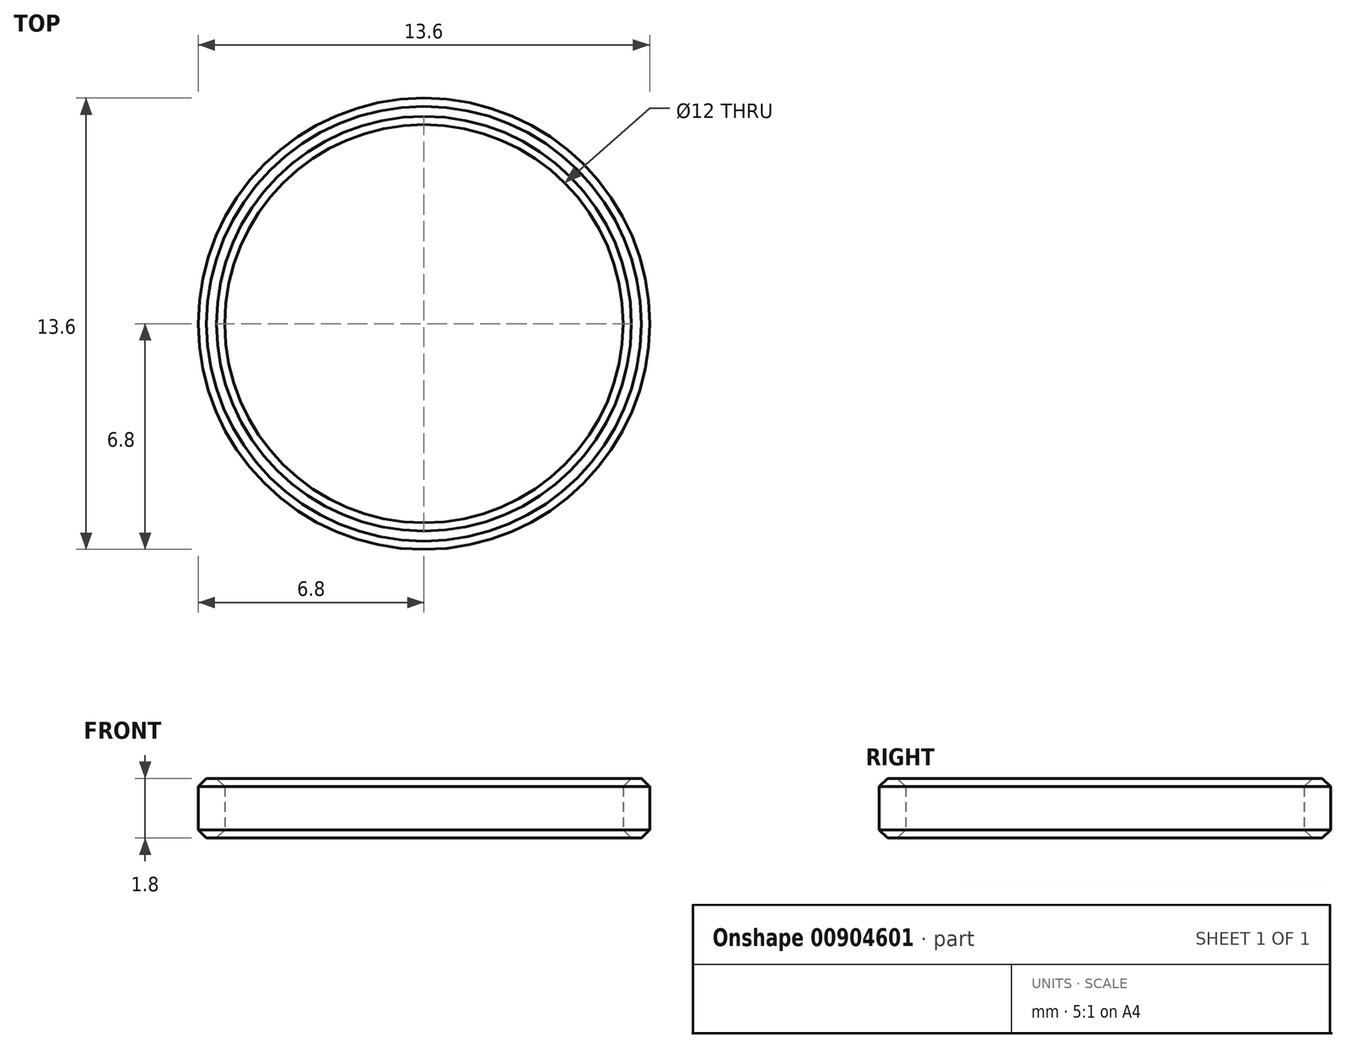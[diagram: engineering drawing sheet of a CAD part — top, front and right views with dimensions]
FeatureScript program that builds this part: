
annotation { "Feature Type Name" : "Feature", "Feature Type Description" : "" }
export const myFeature = defineFeature(function(context is Context, id is Id, definition is map)
    precondition{}
    {
        {
            assignVariable(context, id + "F0", {"name" : "Hauteur", "anyValue" : 1.8});
        }
        {
            var Q0;
            Q0=qCreatedBy(makeId("Top.planeOp"),FACE);
            var sketch = newSketch(context, id + "F1", { "sketchPlane" : qUnion([Q0])});
            skCircle(sketch, "E0", {"center": v(0, 0) * mm, "radius": 6 * mm});
            skCircle(sketch, "E1", {"center": v(0, 0) * mm, "radius": 6.8 * mm});
            skSolve(sketch);
        }
        {
            var Q0;
            Q0=makeQuery(id+"F1.imprint","IMPRINT",FACE,{"disambiguationData":[TD([[makeQuery(id+"F1.imprint","IMPRINT",EDGE,{"derivedFrom":sQuery(id+"F1.wireOp",EDGE,"E0")}),-1.0]])]});
            extrude(context, id + "F2", {"entities" : qUnion([Q0]), "depth" : (getVariable(context, 'Hauteur')) * mm, "offsetDistance" : 25 * mm});
        }
        {
            var Q0;
            Q0=makeQuery(id+"F2.opExtrude","CAP_EDGE",EDGE,{"disambiguationData":[OSD([sQuery(id+"F1.wireOp",EDGE,"E0")])],"isStart":true});
            var Q1;
            Q1=makeQuery(id+"F2.opExtrude","CAP_EDGE",EDGE,{"disambiguationData":[OSD([sQuery(id+"F1.wireOp",EDGE,"E0")])],"isStart":false});
            var Q2;
            Q2=makeQuery(id+"F2.opExtrude","CAP_EDGE",EDGE,{"disambiguationData":[OSD([sQuery(id+"F1.wireOp",EDGE,"E1")])],"isStart":true});
            var Q3;
            Q3=makeQuery(id+"F2.opExtrude","CAP_EDGE",EDGE,{"disambiguationData":[OSD([sQuery(id+"F1.wireOp",EDGE,"E1")])],"isStart":false});
            chamfer(context, id + "F3", {"entities" : qUnion([Q0, Q1, Q2, Q3]), "width" : 0.25 * mm, "tangentPropagation" : true});
        }
    });
